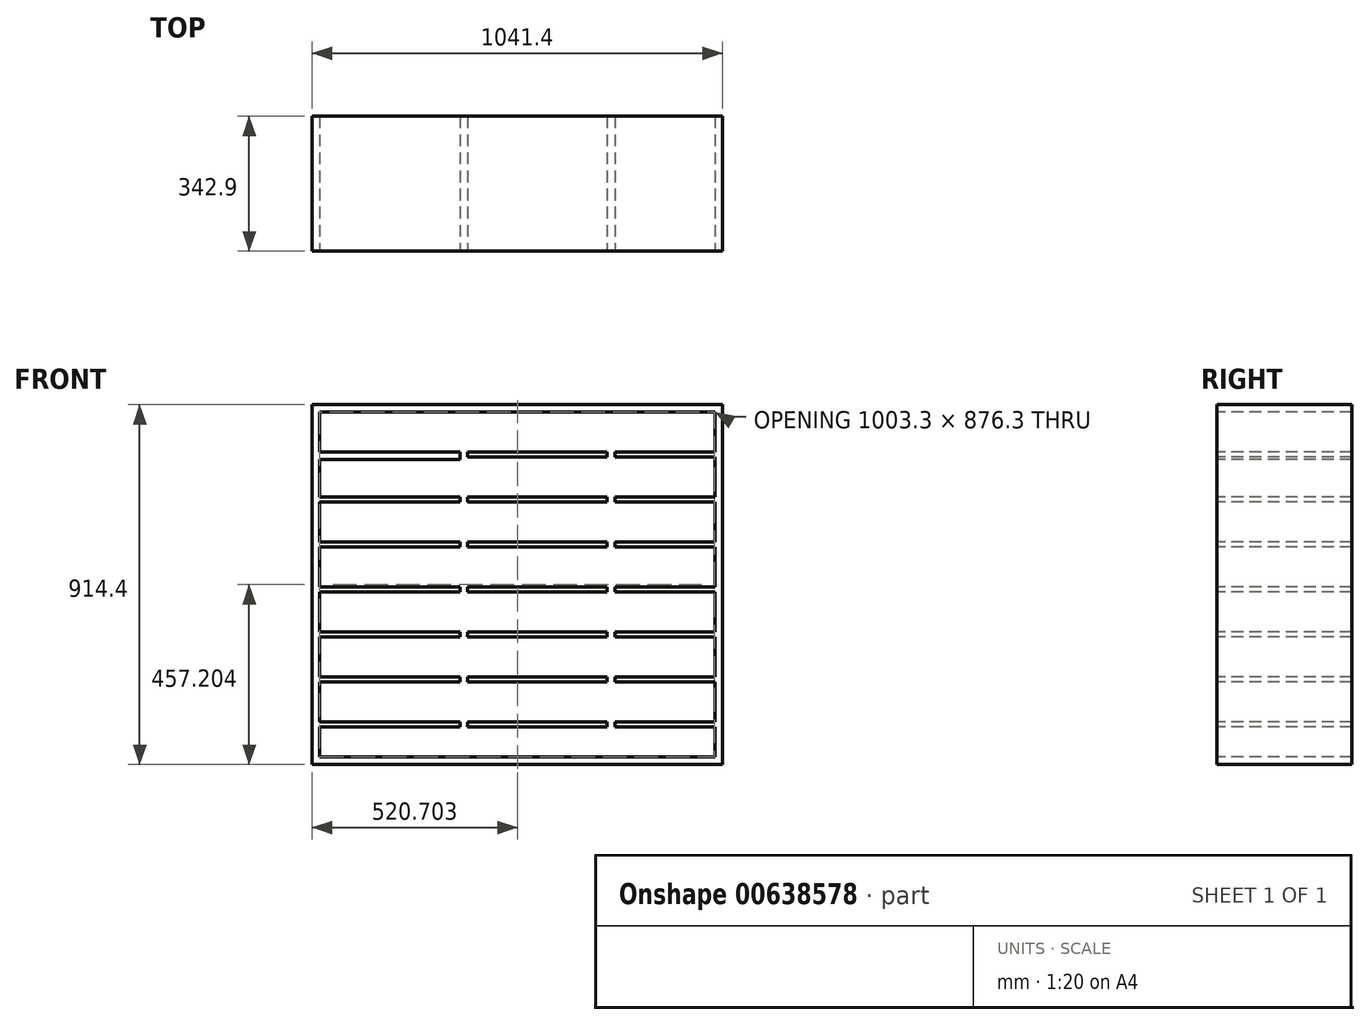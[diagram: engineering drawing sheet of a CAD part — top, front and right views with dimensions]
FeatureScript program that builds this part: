
annotation { "Feature Type Name" : "Feature", "Feature Type Description" : "" }
export const myFeature = defineFeature(function(context is Context, id is Id, definition is map)
    precondition{}
    {
        {
            var Q0;
            Q0=qCreatedBy(makeId("Front.planeOp"),FACE);
            var sketch = newSketch(context, id + "F0", { "sketchPlane" : qUnion([Q0])});
            skLineSegment(sketch, "E0.bottom", {"start": v(-489.12, 699.27) * mm, "end": v(552.28, 699.27) * mm});
            skLineSegment(sketch, "E0.top", {"start": v(-489.12, -215.13) * mm, "end": v(552.28, -215.13) * mm});
            skLineSegment(sketch, "E0.left", {"start": v(-489.12, 699.27) * mm, "end": v(-489.12, -215.13) * mm});
            skLineSegment(sketch, "E0.right", {"start": v(552.28, 699.27) * mm, "end": v(552.28, -215.13) * mm});
            skLineSegment(sketch, "E1", {"start": v(533.23, -196.08) * mm, "end": v(533.23, 680.22) * mm});
            skLineSegment(sketch, "E2", {"start": v(-470.07, 578.62) * mm, "end": v(-470.07, 680.22) * mm});
            skLineSegment(sketch, "E3", {"start": v(-470.07, 680.22) * mm, "end": v(533.23, 680.22) * mm});
            skLineSegment(sketch, "E4", {"start": v(-470.07, -196.08) * mm, "end": v(533.23, -196.08) * mm});
            skLineSegment(sketch, "E5", {"start": v(-114.47, 680.22) * mm, "end": v(-114.47, 578.62) * mm});
            skLineSegment(sketch, "E6", {"start": v(-114.47, 680.22) * mm, "end": v(-95.42, 680.22) * mm});
            skLineSegment(sketch, "E7", {"start": v(-95.42, 680.22) * mm, "end": v(-95.42, -196.08) * mm});
            skLineSegment(sketch, "E8", {"start": v(-95.42, -196.08) * mm, "end": v(-114.47, -196.08) * mm});
            skLineSegment(sketch, "E9", {"start": v(-95.42, 680.22) * mm, "end": v(260.18, 680.22) * mm});
            skLineSegment(sketch, "E10", {"start": v(260.18, 680.22) * mm, "end": v(260.18, -196.08) * mm});
            skLineSegment(sketch, "E11", {"start": v(260.18, 680.22) * mm, "end": v(279.23, 680.22) * mm});
            skLineSegment(sketch, "E12", {"start": v(279.23, 680.22) * mm, "end": v(279.23, -196.08) * mm});
            skLineSegment(sketch, "E13", {"start": v(279.23, -196.08) * mm, "end": v(260.18, -196.08) * mm});
            skLineSegment(sketch, "E14", {"start": v(-470.07, 680.22) * mm, "end": v(-470.07, 578.62) * mm});
            skLineSegment(sketch, "E15", {"start": v(-470.07, 578.62) * mm, "end": v(-114.47, 578.62) * mm});
            skLineSegment(sketch, "E16", {"start": v(-114.47, 578.62) * mm, "end": v(-114.47, 680.22) * mm});
            skLineSegment(sketch, "E17", {"start": v(-470.07, 578.62) * mm, "end": v(-470.07, 559.57) * mm});
            skLineSegment(sketch, "E18", {"start": v(-470.07, 559.57) * mm, "end": v(-114.47, 559.57) * mm});
            skLineSegment(sketch, "E19", {"start": v(-114.47, 559.57) * mm, "end": v(-114.47, 578.62) * mm});
            skLineSegment(sketch, "E20.0.1.0", {"start": v(-114.47, 565.92) * mm, "end": v(-114.47, 464.32) * mm});
            skLineSegment(sketch, "E20.0.1.1", {"start": v(-470.07, 464.32) * mm, "end": v(-470.07, 565.92) * mm});
            skLineSegment(sketch, "E20.0.1.2", {"start": v(-470.07, 464.32) * mm, "end": v(-114.47, 464.32) * mm});
            skLineSegment(sketch, "E20.0.1.3", {"start": v(-470.07, 451.62) * mm, "end": v(-114.47, 451.62) * mm});
            skLineSegment(sketch, "E20.0.2.0", {"start": v(-114.47, 451.62) * mm, "end": v(-114.47, 350.02) * mm});
            skLineSegment(sketch, "E20.0.2.1", {"start": v(-470.07, 350.02) * mm, "end": v(-470.07, 451.62) * mm});
            skLineSegment(sketch, "E20.0.2.2", {"start": v(-470.07, 350.02) * mm, "end": v(-114.47, 350.02) * mm});
            skLineSegment(sketch, "E20.0.2.3", {"start": v(-470.07, 337.32) * mm, "end": v(-114.47, 337.32) * mm});
            skLineSegment(sketch, "E20.0.3.0", {"start": v(-114.47, 337.32) * mm, "end": v(-114.47, 235.72) * mm});
            skLineSegment(sketch, "E20.0.3.1", {"start": v(-470.07, 235.72) * mm, "end": v(-470.07, 337.32) * mm});
            skLineSegment(sketch, "E20.0.3.2", {"start": v(-470.07, 235.72) * mm, "end": v(-114.47, 235.72) * mm});
            skLineSegment(sketch, "E20.0.3.3", {"start": v(-470.07, 223.02) * mm, "end": v(-114.47, 223.02) * mm});
            skLineSegment(sketch, "E20.0.4.0", {"start": v(-114.47, 223.02) * mm, "end": v(-114.47, 121.42) * mm});
            skLineSegment(sketch, "E20.0.4.1", {"start": v(-470.07, 121.42) * mm, "end": v(-470.07, 223.02) * mm});
            skLineSegment(sketch, "E20.0.4.2", {"start": v(-470.07, 121.42) * mm, "end": v(-114.47, 121.42) * mm});
            skLineSegment(sketch, "E20.0.4.3", {"start": v(-470.07, 108.72) * mm, "end": v(-114.47, 108.72) * mm});
            skLineSegment(sketch, "E20.0.5.0", {"start": v(-114.47, 108.72) * mm, "end": v(-114.47, 7.12) * mm});
            skLineSegment(sketch, "E20.0.5.1", {"start": v(-470.07, 7.12) * mm, "end": v(-470.07, 108.72) * mm});
            skLineSegment(sketch, "E20.0.5.2", {"start": v(-470.07, 7.12) * mm, "end": v(-114.47, 7.12) * mm});
            skLineSegment(sketch, "E20.0.5.3", {"start": v(-470.07, -5.58) * mm, "end": v(-114.47, -5.58) * mm});
            skLineSegment(sketch, "E20.0.6.0", {"start": v(-114.47, -5.58) * mm, "end": v(-114.47, -107.18) * mm});
            skLineSegment(sketch, "E20.0.6.1", {"start": v(-470.07, -107.18) * mm, "end": v(-470.07, -5.58) * mm});
            skLineSegment(sketch, "E20.0.6.2", {"start": v(-470.07, -107.18) * mm, "end": v(-114.47, -107.18) * mm});
            skLineSegment(sketch, "E20.0.6.3", {"start": v(-470.07, -119.88) * mm, "end": v(-114.47, -119.88) * mm});
            skLineSegment(sketch, "E20.1.0.0", {"start": v(260.18, 680.22) * mm, "end": v(260.18, 578.62) * mm});
            skLineSegment(sketch, "E20.1.0.1", {"start": v(-95.42, 578.62) * mm, "end": v(-95.42, 680.22) * mm});
            skLineSegment(sketch, "E20.1.0.2", {"start": v(-95.42, 578.62) * mm, "end": v(260.18, 578.62) * mm});
            skLineSegment(sketch, "E20.1.0.3", {"start": v(-95.42, 565.92) * mm, "end": v(260.18, 565.92) * mm});
            skLineSegment(sketch, "E20.1.1.0", {"start": v(260.18, 565.92) * mm, "end": v(260.18, 464.32) * mm});
            skLineSegment(sketch, "E20.1.1.1", {"start": v(-95.42, 464.32) * mm, "end": v(-95.42, 565.92) * mm});
            skLineSegment(sketch, "E20.1.1.2", {"start": v(-95.42, 464.32) * mm, "end": v(260.18, 464.32) * mm});
            skLineSegment(sketch, "E20.1.1.3", {"start": v(-95.42, 451.62) * mm, "end": v(260.18, 451.62) * mm});
            skLineSegment(sketch, "E20.1.2.0", {"start": v(260.18, 451.62) * mm, "end": v(260.18, 350.02) * mm});
            skLineSegment(sketch, "E20.1.2.1", {"start": v(-95.42, 350.02) * mm, "end": v(-95.42, 451.62) * mm});
            skLineSegment(sketch, "E20.1.2.2", {"start": v(-95.42, 350.02) * mm, "end": v(260.18, 350.02) * mm});
            skLineSegment(sketch, "E20.1.2.3", {"start": v(-95.42, 337.32) * mm, "end": v(260.18, 337.32) * mm});
            skLineSegment(sketch, "E20.1.3.0", {"start": v(260.18, 337.32) * mm, "end": v(260.18, 235.72) * mm});
            skLineSegment(sketch, "E20.1.3.1", {"start": v(-95.42, 235.72) * mm, "end": v(-95.42, 337.32) * mm});
            skLineSegment(sketch, "E20.1.3.2", {"start": v(-95.42, 235.72) * mm, "end": v(260.18, 235.72) * mm});
            skLineSegment(sketch, "E20.1.3.3", {"start": v(-95.42, 223.02) * mm, "end": v(260.18, 223.02) * mm});
            skLineSegment(sketch, "E20.1.4.0", {"start": v(260.18, 223.02) * mm, "end": v(260.18, 121.42) * mm});
            skLineSegment(sketch, "E20.1.4.1", {"start": v(-95.42, 121.42) * mm, "end": v(-95.42, 223.02) * mm});
            skLineSegment(sketch, "E20.1.4.2", {"start": v(-95.42, 121.42) * mm, "end": v(260.18, 121.42) * mm});
            skLineSegment(sketch, "E20.1.4.3", {"start": v(-95.42, 108.72) * mm, "end": v(260.18, 108.72) * mm});
            skLineSegment(sketch, "E20.1.5.0", {"start": v(260.18, 108.72) * mm, "end": v(260.18, 7.12) * mm});
            skLineSegment(sketch, "E20.1.5.1", {"start": v(-95.42, 7.12) * mm, "end": v(-95.42, 108.72) * mm});
            skLineSegment(sketch, "E20.1.5.2", {"start": v(-95.42, 7.12) * mm, "end": v(260.18, 7.12) * mm});
            skLineSegment(sketch, "E20.1.5.3", {"start": v(-95.42, -5.58) * mm, "end": v(260.18, -5.58) * mm});
            skLineSegment(sketch, "E20.1.6.0", {"start": v(260.18, -5.58) * mm, "end": v(260.18, -107.18) * mm});
            skLineSegment(sketch, "E20.1.6.1", {"start": v(-95.42, -107.18) * mm, "end": v(-95.42, -5.58) * mm});
            skLineSegment(sketch, "E20.1.6.2", {"start": v(-95.42, -107.18) * mm, "end": v(260.18, -107.18) * mm});
            skLineSegment(sketch, "E20.1.6.3", {"start": v(-95.42, -119.88) * mm, "end": v(260.18, -119.88) * mm});
            skLineSegment(sketch, "E20.2.0.1", {"start": v(279.23, 578.62) * mm, "end": v(279.23, 680.22) * mm});
            skLineSegment(sketch, "E20.2.0.2", {"start": v(279.23, 578.62) * mm, "end": v(533.23, 578.62) * mm});
            skLineSegment(sketch, "E20.2.0.3", {"start": v(279.23, 565.92) * mm, "end": v(533.23, 565.92) * mm});
            skLineSegment(sketch, "E20.2.1.1", {"start": v(279.23, 464.32) * mm, "end": v(279.23, 565.92) * mm});
            skLineSegment(sketch, "E20.2.1.2", {"start": v(279.23, 464.32) * mm, "end": v(533.23, 464.32) * mm});
            skLineSegment(sketch, "E20.2.1.3", {"start": v(279.23, 451.62) * mm, "end": v(533.23, 451.62) * mm});
            skLineSegment(sketch, "E20.2.2.1", {"start": v(279.23, 350.02) * mm, "end": v(279.23, 451.62) * mm});
            skLineSegment(sketch, "E20.2.2.2", {"start": v(279.23, 350.02) * mm, "end": v(533.23, 350.02) * mm});
            skLineSegment(sketch, "E20.2.2.3", {"start": v(279.23, 337.32) * mm, "end": v(533.23, 337.32) * mm});
            skLineSegment(sketch, "E20.2.3.1", {"start": v(279.23, 235.72) * mm, "end": v(279.23, 337.32) * mm});
            skLineSegment(sketch, "E20.2.3.3", {"start": v(279.23, 223.02) * mm, "end": v(533.23, 223.02) * mm});
            skLineSegment(sketch, "E20.2.4.1", {"start": v(279.23, 121.42) * mm, "end": v(279.23, 223.02) * mm});
            skLineSegment(sketch, "E20.2.4.2", {"start": v(279.23, 121.42) * mm, "end": v(533.23, 121.42) * mm});
            skLineSegment(sketch, "E20.2.4.3", {"start": v(279.23, 108.72) * mm, "end": v(533.23, 108.72) * mm});
            skLineSegment(sketch, "E20.2.5.1", {"start": v(279.23, 7.12) * mm, "end": v(279.23, 108.72) * mm});
            skLineSegment(sketch, "E20.2.5.2", {"start": v(279.23, 7.12) * mm, "end": v(533.23, 7.12) * mm});
            skLineSegment(sketch, "E20.2.5.3", {"start": v(279.23, -5.58) * mm, "end": v(533.23, -5.58) * mm});
            skLineSegment(sketch, "E20.2.6.1", {"start": v(279.23, -107.18) * mm, "end": v(279.23, -5.58) * mm});
            skLineSegment(sketch, "E20.2.6.3", {"start": v(279.23, -119.88) * mm, "end": v(533.23, -119.88) * mm});
            skLineSegment(sketch, "E20.direction2", {"start": v(-114.47, 578.62) * mm, "end": v(-114.47, 464.32) * mm, "construction": true});
            skLineSegment(sketch, "E21", {"start": v(279.23, 235.72) * mm, "end": v(533.23, 235.72) * mm});
            skLineSegment(sketch, "E22", {"start": v(-470.07, 464.32) * mm, "end": v(-470.07, -196.08) * mm});
            skLineSegment(sketch, "E23", {"start": v(279.23, -107.18) * mm, "end": v(533.23, -107.18) * mm});
            skLineSegment(sketch, "E24", {"start": v(-114.47, -119.88) * mm, "end": v(-114.47, -196.08) * mm});
            skLineSegment(sketch, "E25", {"start": v(-114.47, -119.88) * mm, "end": v(-114.47, 464.32) * mm});
            skSolve(sketch);
        }
        {
            var Q0;
            Q0=makeQuery(id+"F0.imprint","IMPRINT",FACE,{"disambiguationData":[TD([[makeQuery(id+"F0.imprint","IMPRINT",EDGE,{"derivedFrom":sQuery(id+"F0.wireOp",EDGE,"E0.bottom")}),-1.0]])]});
            var Q1;
            Q1=makeQuery(id+"F0.imprint","IMPRINT",FACE,{"disambiguationData":[TD([[makeQuery(id+"F0.imprint","IMPRINT",EDGE,{"derivedFrom":sQuery(id+"F0.wireOp",EDGE,"E15")}),-1.0]])]});
            var Q2;
            Q2=makeQuery(id+"F0.imprint","IMPRINT",FACE,{"disambiguationData":[TD([[makeQuery(id+"F0.imprint","IMPRINT",EDGE,{"derivedFrom":sQuery(id+"F0.wireOp",EDGE,"E6")}),-1.0]])]});
            var Q3;
            Q3=makeQuery(id+"F0.imprint","IMPRINT",FACE,{"disambiguationData":[TD([[makeQuery(id+"F0.imprint","IMPRINT",EDGE,{"derivedFrom":sQuery(id+"F0.wireOp",EDGE,"E11")}),-1.0]])]});
            var Q4;
            {var subQ0=sQuery(id+"F0.wireOp",EDGE,"E20.1.0.2");Q4=makeQuery(id+"F0.imprint","IMPRINT",FACE,{"disambiguationData":[TD([[makeQuery(id+"F0.imprint","IMPRINT",EDGE,{"derivedFrom":subQ0}),-1.0]])]});}
            var Q5;
            {var subQ0=sQuery(id+"F0.wireOp",EDGE,"E20.2.0.2");Q5=makeQuery(id+"F0.imprint","IMPRINT",FACE,{"disambiguationData":[TD([[makeQuery(id+"F0.imprint","IMPRINT",EDGE,{"derivedFrom":subQ0}),-1.0]])]});}
            var Q6;
            {var subQ0=sQuery(id+"F0.wireOp",EDGE,"E20.2.1.2");Q6=makeQuery(id+"F0.imprint","IMPRINT",FACE,{"disambiguationData":[TD([[makeQuery(id+"F0.imprint","IMPRINT",EDGE,{"derivedFrom":subQ0}),-1.0]])]});}
            var Q7;
            {var subQ0=sQuery(id+"F0.wireOp",EDGE,"E20.1.1.2");Q7=makeQuery(id+"F0.imprint","IMPRINT",FACE,{"disambiguationData":[TD([[makeQuery(id+"F0.imprint","IMPRINT",EDGE,{"derivedFrom":subQ0}),-1.0]])]});}
            var Q8;
            {var subQ0=sQuery(id+"F0.wireOp",EDGE,"E20.0.1.2");Q8=makeQuery(id+"F0.imprint","IMPRINT",FACE,{"disambiguationData":[TD([[makeQuery(id+"F0.imprint","IMPRINT",EDGE,{"derivedFrom":subQ0}),-1.0]])]});}
            var Q9;
            {var subQ0=sQuery(id+"F0.wireOp",EDGE,"E20.0.2.2");Q9=makeQuery(id+"F0.imprint","IMPRINT",FACE,{"disambiguationData":[TD([[makeQuery(id+"F0.imprint","IMPRINT",EDGE,{"derivedFrom":subQ0}),-1.0]])]});}
            var Q10;
            {var subQ0=sQuery(id+"F0.wireOp",EDGE,"E20.0.4.2");Q10=makeQuery(id+"F0.imprint","IMPRINT",FACE,{"disambiguationData":[TD([[makeQuery(id+"F0.imprint","IMPRINT",EDGE,{"derivedFrom":subQ0}),-1.0]])]});}
            var Q11;
            {var subQ0=sQuery(id+"F0.wireOp",EDGE,"E20.0.5.2");Q11=makeQuery(id+"F0.imprint","IMPRINT",FACE,{"disambiguationData":[TD([[makeQuery(id+"F0.imprint","IMPRINT",EDGE,{"derivedFrom":subQ0}),-1.0]])]});}
            var Q12;
            {var subQ0=sQuery(id+"F0.wireOp",EDGE,"E20.0.6.2");Q12=makeQuery(id+"F0.imprint","IMPRINT",FACE,{"disambiguationData":[TD([[makeQuery(id+"F0.imprint","IMPRINT",EDGE,{"derivedFrom":subQ0}),-1.0]])]});}
            var Q13;
            {var subQ0=sQuery(id+"F0.wireOp",EDGE,"E20.1.6.2");Q13=makeQuery(id+"F0.imprint","IMPRINT",FACE,{"disambiguationData":[TD([[makeQuery(id+"F0.imprint","IMPRINT",EDGE,{"derivedFrom":subQ0}),-1.0]])]});}
            var Q14;
            {var subQ0=sQuery(id+"F0.wireOp",EDGE,"E20.1.5.2");Q14=makeQuery(id+"F0.imprint","IMPRINT",FACE,{"disambiguationData":[TD([[makeQuery(id+"F0.imprint","IMPRINT",EDGE,{"derivedFrom":subQ0}),-1.0]])]});}
            var Q15;
            {var subQ0=sQuery(id+"F0.wireOp",EDGE,"E20.1.4.2");Q15=makeQuery(id+"F0.imprint","IMPRINT",FACE,{"disambiguationData":[TD([[makeQuery(id+"F0.imprint","IMPRINT",EDGE,{"derivedFrom":subQ0}),-1.0]])]});}
            var Q16;
            {var subQ0=sQuery(id+"F0.wireOp",EDGE,"E20.1.2.2");Q16=makeQuery(id+"F0.imprint","IMPRINT",FACE,{"disambiguationData":[TD([[makeQuery(id+"F0.imprint","IMPRINT",EDGE,{"derivedFrom":subQ0}),-1.0]])]});}
            var Q17;
            {var subQ0=sQuery(id+"F0.wireOp",EDGE,"E20.1.3.2");Q17=makeQuery(id+"F0.imprint","IMPRINT",FACE,{"disambiguationData":[TD([[makeQuery(id+"F0.imprint","IMPRINT",EDGE,{"derivedFrom":subQ0}),-1.0]])]});}
            var Q18;
            {var subQ0=sQuery(id+"F0.wireOp",EDGE,"E20.2.2.2");Q18=makeQuery(id+"F0.imprint","IMPRINT",FACE,{"disambiguationData":[TD([[makeQuery(id+"F0.imprint","IMPRINT",EDGE,{"derivedFrom":subQ0}),-1.0]])]});}
            var Q19;
            {var subQ0=sQuery(id+"F0.wireOp",EDGE,"E20.2.3.3");Q19=makeQuery(id+"F0.imprint","IMPRINT",FACE,{"disambiguationData":[TD([[makeQuery(id+"F0.imprint","IMPRINT",EDGE,{"derivedFrom":subQ0}),1.0]])]});}
            var Q20;
            {var subQ0=sQuery(id+"F0.wireOp",EDGE,"E20.2.4.2");Q20=makeQuery(id+"F0.imprint","IMPRINT",FACE,{"disambiguationData":[TD([[makeQuery(id+"F0.imprint","IMPRINT",EDGE,{"derivedFrom":subQ0}),-1.0]])]});}
            var Q21;
            {var subQ0=sQuery(id+"F0.wireOp",EDGE,"E20.2.5.2");Q21=makeQuery(id+"F0.imprint","IMPRINT",FACE,{"disambiguationData":[TD([[makeQuery(id+"F0.imprint","IMPRINT",EDGE,{"derivedFrom":subQ0}),-1.0]])]});}
            var Q22;
            {var subQ0=sQuery(id+"F0.wireOp",EDGE,"E20.2.6.3");Q22=makeQuery(id+"F0.imprint","IMPRINT",FACE,{"disambiguationData":[TD([[makeQuery(id+"F0.imprint","IMPRINT",EDGE,{"derivedFrom":subQ0}),1.0]])]});}
            var Q23;
            {var subQ0=sQuery(id+"F0.wireOp",EDGE,"E20.0.3.2");Q23=makeQuery(id+"F0.imprint","IMPRINT",FACE,{"disambiguationData":[TD([[makeQuery(id+"F0.imprint","IMPRINT",EDGE,{"derivedFrom":subQ0}),-1.0]])]});}
            extrude(context, id + "F1", {"entities" : qUnion([Q0, Q1, Q2, Q3, Q4, Q5, Q6, Q7, Q8, Q9, Q10, Q11, Q12, Q13, Q14, Q15, Q16, Q17, Q18, Q19, Q20, Q21, Q22, Q23]), "oppositeDirection" : true, "depth" : 342.9 * mm, "offsetDistance" : 25.4 * mm});
        }
    });
